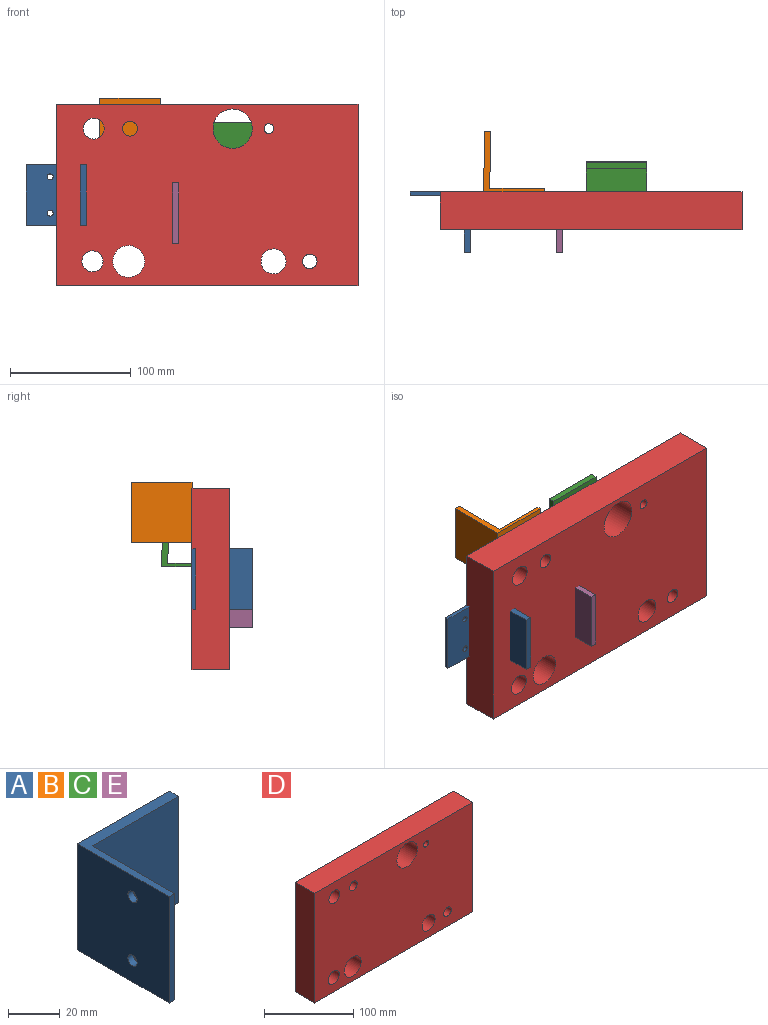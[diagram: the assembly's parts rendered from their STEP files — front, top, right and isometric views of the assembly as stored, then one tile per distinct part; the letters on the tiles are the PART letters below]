
ASSEMBLY  parts=5 mates=4
PART A: 10 faces, bbox 50x50x50 mm
  f0: plane 50x46.89mm, normal (0,-1,0), area 2344.3mm2, adj f1,f5,f6,f7
  f1: plane 50x4.99mm, normal (1,-0.02,0), area 249.4mm2, adj f0,f2,f6,f7
  f2: plane 50x50mm, normal (0,1,0), area 2500mm2, adj f1,f3,f6,f7
  f3: plane 50x50mm, normal (-1,0,0), area 2460.7mm2, adj f2,f4,f6,f7,f8,f9
  f4: plane 50x3mm, normal (0,-1,0), area 150mm2, adj f3,f5,f6,f7
  f5: plane 50x45mm, normal (1,0,0), area 2210.7mm2, adj f0,f4,f6,f7,f8,f9
  f6: plane 50x50mm, normal (0,0,1), area 384.1mm2, adj f0,f1,f2,f3,f4,f5
  f7: plane 50x50mm, normal (0,0,-1), area 384.1mm2, adj f0,f1,f2,f3,f4,f5
  f8: cylinder r=2.5mm len=5mm, axis (1,0,0), area 47.1mm2, adj f3,f5
  f9: cylinder r=2.5mm len=5mm, axis (1,0,0), area 47.1mm2, adj f3,f5
PART B: same geometry as A
PART C: same geometry as A
PART D: 14 faces, bbox 250x31x150 mm
  f0: plane 150x31mm, normal (1,0,0), area 4650mm2, adj f1,f11,f12,f13
  f1: plane 250x31mm, normal (0,0,1), area 7750mm2, adj f0,f2,f12,f13
  f2: plane 150x31mm, normal (-1,0,0), area 4650mm2, adj f1,f11,f12,f13
  f3: cylinder r=8.67mm len=31mm, axis (0,1,0), area 1687.9mm2, adj f12,f13
  f4: cylinder r=6.13mm len=31mm, axis (0,1,0), area 1193.6mm2, adj f12,f13
  f5: cylinder r=16.3mm len=32.6mm, axis (0,1,0), area 3174.4mm2, adj f12,f13
  f6: cylinder r=4mm len=31mm, axis (0,1,0), area 779.1mm2, adj f12,f13
  f7: cylinder r=8.75mm len=31mm, axis (0,1,0), area 1704mm2, adj f12,f13
  f8: cylinder r=13.21mm len=31mm, axis (0,1,0), area 2573.6mm2, adj f12,f13
  f9: cylinder r=10.37mm len=31mm, axis (0,1,0), area 2020.6mm2, adj f12,f13
  f10: cylinder r=6.04mm len=31mm, axis (0,1,0), area 1176.3mm2, adj f12,f13
  f11: plane 250x31mm, normal (0,0,-1), area 7750mm2, adj f0,f2,f12,f13
  f12: plane 250x150mm, normal (0,1,0), area 35019.8mm2, adj f0,f1,f2,f3,f4,f5,f6,f7
  f13: plane 250x150mm, normal (0,-1,0), area 35019.8mm2, adj f0,f1,f2,f3,f4,f5,f6,f7
PART E: same geometry as A
PLACE A rot(axis=(0,0,-1),90deg) t=(-188.2,-407.69,91.99)mm
PLACE B rot(axis=(0,0,1),90deg) t=(-161.09,-298.88,146.99)mm
PLACE C rot(axis=(0,-1,0),90deg) t=(-34.05,-336.31,181.39)mm fixed
PLACE D t=(-80.18,-353.28,116.99)mm
PLACE E rot(axis=(0.71,-0.71,0),180deg) t=(-101.1,-407.69,126.99)mm
MATE planar C.f3 <-> E.f7  axis (0,0,-1) through (-59.05,-353.28,126.99)mm
MATE planar B.f3 <-> D.f4  axis (0,-1,0) through (-144.11,-353.28,171.99)mm
MATE planar E.f8 <-> D.f12  axis (0,1,0) through (-79.05,-353.28,116.99)mm
MATE planar A.f3 <-> D.f12  axis (0,1,0) through (-205.18,-353.28,116.99)mm
